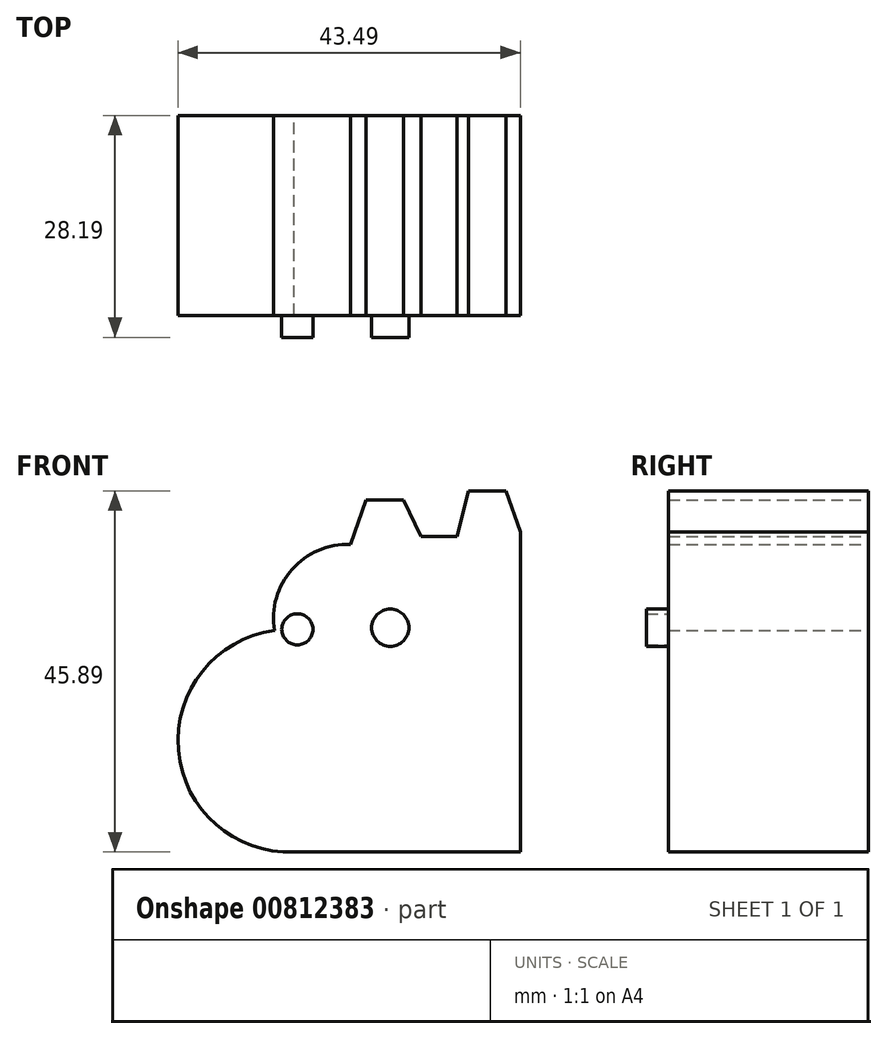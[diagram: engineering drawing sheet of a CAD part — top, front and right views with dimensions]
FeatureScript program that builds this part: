
annotation { "Feature Type Name" : "Feature", "Feature Type Description" : "" }
export const myFeature = defineFeature(function(context is Context, id is Id, definition is map)
    precondition{}
    {
        {
            var Q0;
            Q0=qCreatedBy(makeId("Front.planeOp"),FACE);
            var sketch = newSketch(context, id + "F0", { "sketchPlane" : qUnion([Q0])});
            skCircle(sketch, "E0", {"center": v(-14.52, 0) * mm, "radius": 14.13 * mm});
            skLineSegment(sketch, "E1", {"start": v(-15.12, -14.11) * mm, "end": v(14.85, -14.11) * mm});
            skLineSegment(sketch, "E2", {"start": v(14.85, -14.11) * mm, "end": v(14.85, 6.2) * mm});
            skLineSegment(sketch, "E3", {"start": v(14.85, 6.2) * mm, "end": v(14.85, 26.53) * mm});
            skLineSegment(sketch, "E4", {"start": v(14.85, 26.53) * mm, "end": v(13.06, 31.76) * mm});
            skLineSegment(sketch, "E5", {"start": v(13.06, 31.76) * mm, "end": v(8.28, 31.76) * mm});
            skLineSegment(sketch, "E6", {"start": v(8.28, 31.76) * mm, "end": v(6.78, 25.95) * mm});
            skLineSegment(sketch, "E7", {"start": v(6.78, 25.95) * mm, "end": v(2.24, 25.95) * mm});
            skLineSegment(sketch, "E8", {"start": v(2.24, 25.95) * mm, "end": v(0, 30.6) * mm});
            skLineSegment(sketch, "E9", {"start": v(0, 30.6) * mm, "end": v(-4.77, 30.6) * mm});
            skLineSegment(sketch, "E10", {"start": v(-6.72, 24.94) * mm, "end": v(-4.77, 30.6) * mm});
            skArc(sketch, "E11", {"start": v(-6.72, 24.94) * mm, "mid": v(-14.16, 21.77) * mm, "end": v(-16.38, 14) * mm});
            skSolve(sketch);
        }
        {
            var Q0;
            Q0 = qSketchRegion(id + "F0", true);
            extrude(context, id + "F1", {"entities" : qUnion([Q0]), "depth" : 25.4 * mm, "offsetDistance" : 25.4 * mm});
        }
        {
            var Q0;
            Q0=qCreatedBy(makeId("Front.planeOp"),FACE);
            var sketch = newSketch(context, id + "F2", { "sketchPlane" : qUnion([Q0])});
            skCircle(sketch, "E12", {"center": v(-13.48, 14.17) * mm, "radius": 1.98 * mm});
            skCircle(sketch, "E13", {"center": v(-1.67, 14.37) * mm, "radius": 2.37 * mm});
            skSolve(sketch);
        }
        {
            var Q0;
            Q0 = qSketchRegion(id + "F2", true);
            extrude(context, id + "F3", {"entities" : qUnion([Q0]), "operationType" : NewBodyOperationType.ADD, "depth" : 28.2 * mm, "offsetDistance" : 25.4 * mm});
        }
    });
